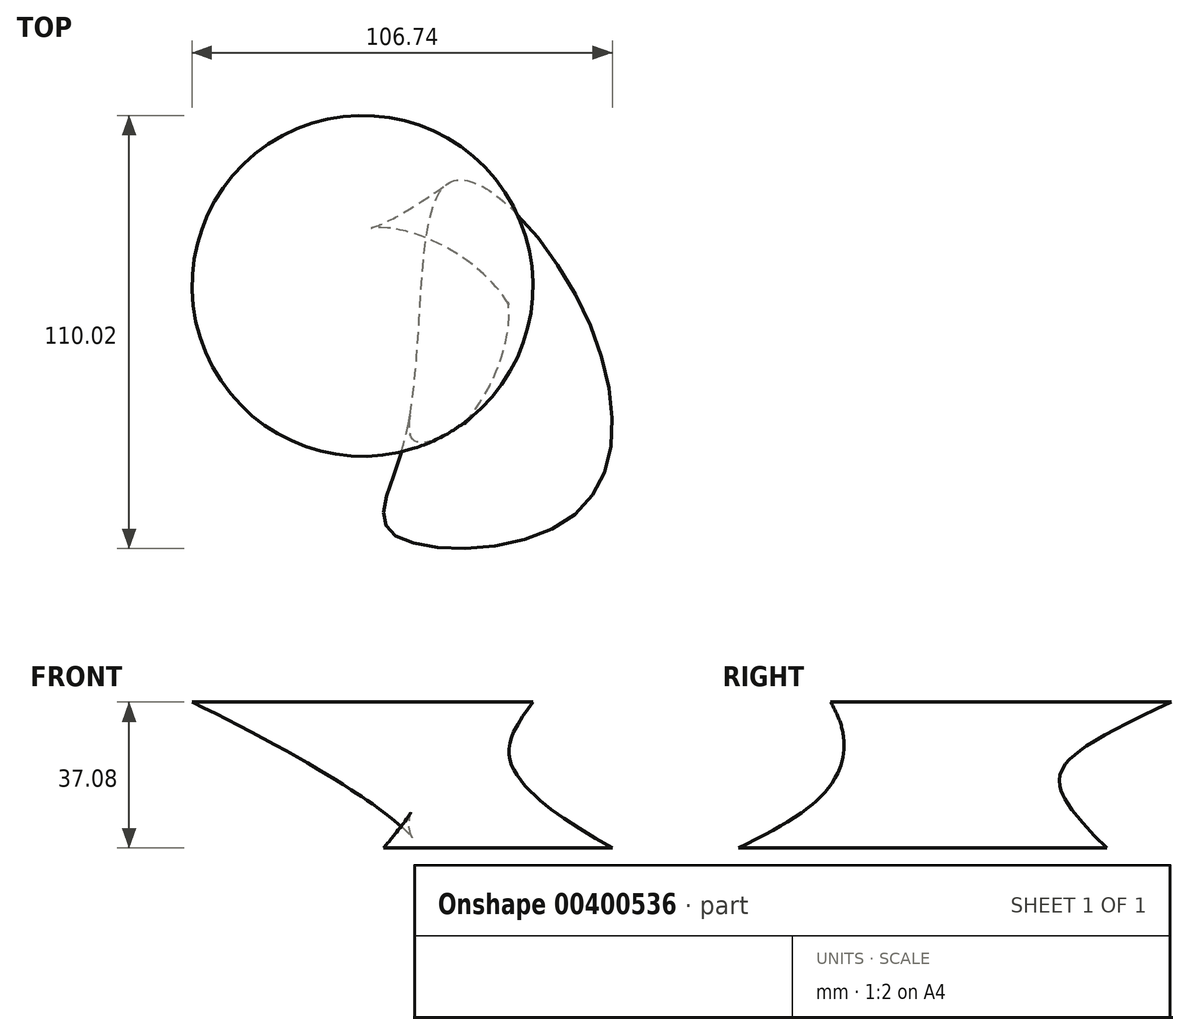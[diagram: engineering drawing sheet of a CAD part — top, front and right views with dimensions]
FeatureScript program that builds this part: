
annotation { "Feature Type Name" : "Feature", "Feature Type Description" : "" }
export const myFeature = defineFeature(function(context is Context, id is Id, definition is map)
    precondition{}
    {
        {
            var Q0;
            Q0=qCreatedBy(makeId("Top.planeOp"),FACE);
            cPlane(context, id + "F0", {"entities" : qUnion([Q0]), "cplaneType" : CPlaneType.OFFSET, "offset" : 37.08 * mm, "width" : 152.4 * mm, "height" : 152.4 * mm});
        }
        {
            var Q0;
            Q0=qCreatedBy(id+"F0.planeOp",FACE);
            var sketch = newSketch(context, id + "F1", { "sketchPlane" : qUnion([Q0])});
            skCircle(sketch, "E0", {"center": v(-11.47, 5.22) * mm, "radius": 43.3 * mm});
            skSolve(sketch);
        }
        {
            var Q0;
            Q0=qCreatedBy(makeId("Top.planeOp"),FACE);
            var sketch = newSketch(context, id + "F2", { "sketchPlane" : qUnion([Q0])});
            skFitSpline(sketch, "E1", {"points": [v(0, -30.68) * mm, v(10.42, 31.4) * mm, v(44.16, 0) * mm, v(41.77, -53.43) * mm, v(-4.21, -57.42) * mm, v(0, -30.68) * mm]});
            skSolve(sketch);
        }
        {
            var Q0;
            Q0 = qSketchRegion(id + "F2", true);
            var Q1;
            Q1 = qSketchRegion(id + "F1", true);
            loft(context, id + "F3", {"sheetProfilesArray" : [{ "sheetProfileEntities" : qUnion([Q0]) }, { "sheetProfileEntities" : qUnion([Q1]) }]});
        }
    });
